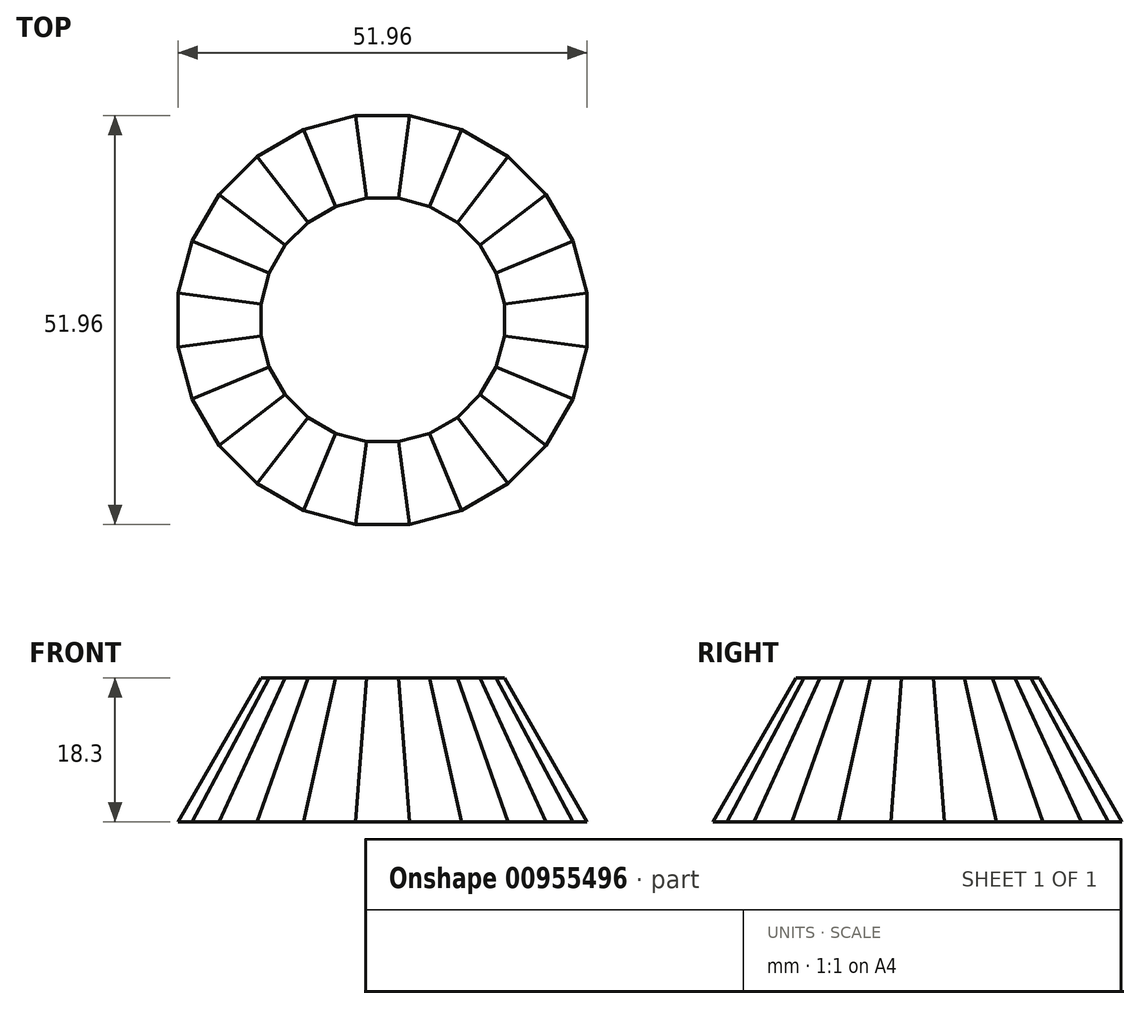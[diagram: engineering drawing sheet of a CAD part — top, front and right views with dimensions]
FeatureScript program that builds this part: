
annotation { "Feature Type Name" : "Feature", "Feature Type Description" : "" }
export const myFeature = defineFeature(function(context is Context, id is Id, definition is map)
    precondition{}
    {
        {
            var Q0;
            Q0=qCreatedBy(makeId("Top.planeOp"),FACE);
            var sketch = newSketch(context, id + "F0", { "sketchPlane" : qUnion([Q0])});
            skLineSegment(sketch, "E0", {"start": v(0, 0) * mm, "end": v(0, -15.6) * mm, "construction": true});
            skArc(sketch, "E1", {"start": v(-2.04, -15.47) * mm, "mid": v(0, -15.6) * mm, "end": v(2.04, -15.47) * mm, "construction": true});
            skPoint(sketch, "E2", {"position": v(0, -15.6) * mm});
            skLineSegment(sketch, "E3", {"start": v(-2.04, -15.47) * mm, "end": v(0, 0) * mm, "construction": true});
            skLineSegment(sketch, "E4", {"start": v(2.04, -15.47) * mm, "end": v(0, 0) * mm, "construction": true});
            skLineSegment(sketch, "E5", {"start": v(-2.04, -15.47) * mm, "end": v(2.04, -15.47) * mm});
            skSolve(sketch);
        }
        {
            var Q0;
            Q0=qCreatedBy(makeId("Top.planeOp"),FACE);
            cPlane(context, id + "F1", {"entities" : qUnion([Q0]), "cplaneType" : CPlaneType.OFFSET, "offset" : 18.3 * mm, "oppositeDirection" : true, "width" : 150 * mm, "height" : 150 * mm});
        }
        {
            var Q0;
            Q0=qCreatedBy(id+"F1.planeOp",FACE);
            var sketch = newSketch(context, id + "F2", { "sketchPlane" : qUnion([Q0])});
            skPoint(sketch, "E6.0", {"position": v(0, 0) * mm});
            skLineSegment(sketch, "E7", {"start": v(0, 0) * mm, "end": v(0, -26.2) * mm, "construction": true});
            skArc(sketch, "E8", {"start": v(-3.42, -25.98) * mm, "mid": v(0, -26.2) * mm, "end": v(3.42, -25.98) * mm, "construction": true});
            skPoint(sketch, "E9", {"position": v(0, -26.2) * mm});
            skLineSegment(sketch, "E10", {"start": v(-3.42, -25.98) * mm, "end": v(0, 0) * mm, "construction": true});
            skLineSegment(sketch, "E11", {"start": v(3.42, -25.98) * mm, "end": v(0, 0) * mm, "construction": true});
            skLineSegment(sketch, "E12", {"start": v(-3.42, -25.98) * mm, "end": v(3.42, -25.98) * mm});
            skSolve(sketch);
        }
        {
            var Q0;
            Q0=qCreatedBy(makeId("Front.planeOp"),FACE);
            var sketch = newSketch(context, id + "F3", { "sketchPlane" : qUnion([Q0])});
            skPoint(sketch, "E13.0", {"position": v(0, -18.3) * mm});
            skLineSegment(sketch, "E14", {"start": v(0, 0) * mm, "end": v(0, -18.3) * mm, "construction": true});
            skSolve(sketch);
        }
        {
            var Q0;
            Q0=sQuery(id+"F0.wireOp",EDGE,"E5");
            var Q1;
            Q1=sQuery(id+"F2.wireOp",EDGE,"E12");
            loft(context, id + "F4", {"bodyType" : ToolBodyType.SURFACE, "wireProfilesArray" : [{ "wireProfileEntities" : qUnion([Q0]) }, { "wireProfileEntities" : qUnion([Q1]) }]});
        }
        {
            var Q0;
            Q0=makeQuery(id+"F4.opLoft","SWEPT_FACE",FACE,{"disambiguationData":[OSD([sQuery(id+"F0.wireOp",VERTEX,"E5.start"),sQuery(id+"F0.wireOp",VERTEX,"E5.end"),sQuery(id+"F0.wireOp",EDGE,"E5"),sQuery(id+"F2.wireOp",VERTEX,"E12.start"),sQuery(id+"F2.wireOp",VERTEX,"E12.end"),sQuery(id+"F2.wireOp",EDGE,"E12")])]});
            var Q1;
            Q1=sQuery(id+"F3.wireOp",EDGE,"E14");
            circularPattern(context, id + "F5", {"patternType" : PatternType.FACE, "faces" : qUnion([Q0]), "axis" : qUnion([Q1]), "angle" : 360 * degree, "instanceCount" : 24, "equalSpace" : true});
        }
    });
